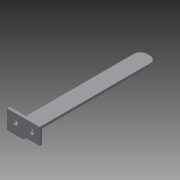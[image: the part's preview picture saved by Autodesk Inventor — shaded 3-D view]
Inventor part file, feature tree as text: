
AUTODESK INVENTOR PART (.ipt)
format: ipt  version: 2015 (Build 190159000, 159)  size: 132,608 bytes
history: native  units: mm
features: sketch x5, extrude x4, other x1, fillet x1, hole x1
ambient origin geometry x8: Origin, YZ Plane, XZ Plane, XY Plane, X Axis, Y Axis, Z Axis, Center Point
bodies: Body1 (feature_tree)
feature tree (12):
  other  "ソリッド1"
  extrude  "押し出し1"  Depth=10.0mm
  fillet  "フィレット1"  Radius=80.0mm
  extrude  "押し出し2"  Depth=1.5mm TaperAngle=0.0deg
  extrude  "押し出し4"  Depth=4.0mm
  extrude  "押し出し6"  Depth=1.5mm TaperAngle=0.0deg
  hole  "穴1"  [1 undecoded]
  sketch  "スケッチ1"
  sketch  "スケッチ2"
  sketch  "スケッチ4"
  sketch  "スケッチ6"
  sketch  "スケッチ8"
note: 1 required parameter value undecoded (feature->parameter linkage not recoverable at this tier; creation-order binding heuristic only, values carry confidence <= 0.55)
